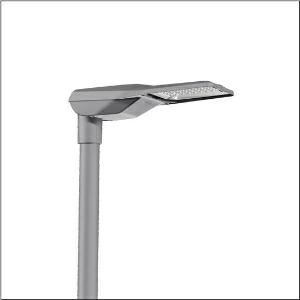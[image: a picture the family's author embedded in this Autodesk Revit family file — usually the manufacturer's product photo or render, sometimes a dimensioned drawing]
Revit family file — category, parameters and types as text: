
# Revit family: streetlight_sl_21_mini___st1_5a_5xe6p43a08hb_28db
name_source: partatom
category: Lighting Fixtures
units: mm (PartAtom-declared; Revit-internal decimal feet)

## family parameters
Cut with Voids When Loaded = No
Host = Face
Light Source = No
Part Type = Normal
Room Calculation Point = No
Round Connector Dimension = Use Diameter
Shared = No

## types (1)
- --- (1 x LED, 9260 lm, 66 W, 4000K)
    Apparent Load = 66 VA
    CIE Flux Codes = 22 53 95 100 100
    Color Rendering = 70
    Color Temperature = 4000K
    Default Elevation = 1800 mm
    Description = Streetlight SL 21 mini, mast luminaire, primary light control with lens, of PMMA, primary optical cover: cover, of toughened safety glass, transparent, light distribution: ST1.5a, light emission: direct distribution, primary light characteristic: asymmetric, installation type: post-top, side-entry, LED, 3G 1.5mm², High Power LED, rated luminous flux: 9.260lm, luminous efficacy: 140lm/W, light colour: 740, colour temperature: 4000K, control: overheat protection, constant luminous flux control, time-dependent luminous flux control, flexible luminous flux parameterisation, mains connection: 230..240V, AC, 50/60Hz, connection cable pre-assembled, cable length: 8,5m, wiring characteristics: H07RN-F, start of lifetime: 66W, end of service life: 69W, reduction: 30W, luminaire housing, of diecast aluminium, powder-coated, Siteco® metallic grey (DB 702S), corrosivity category C5 mid according to DIN EN ISO 12944, please order mast flange separately, inclination adjustable: 0°, 5°, 10°, 15°, sealing non-destructively replaceable, multi-level sealing system, length: 628mm, width: 235mm, height: 110mm, mast flange for spigot size: 42mm (side-entry): 5XC10008XM4, 60/48mm (side-entry/post-top): 5XC10108XM2, 76/60mm (side-entry/post-top): 5XC10108XM1, protection rating (complete): IP66, insulation class (complete): insulation class II (safety insulation), certification: CE, ENEC, ENEC+, VDE, impact resistance: IK09, permissible operating ambient temperature for outdoor applications: -40..+50°C, standard-compliant lighting for roads and squares, packaging unit: 1 piece

Light Distribution: ST1.5a
    Height = 110 mm
    Lamp = 1 x LED
    Lamp Light Flux = 9260 lm
    Lamp Power = 66 W
    Lamp count = 1
    Length = 625 mm
    Luminous efficacy = 140 lm/W
    Manufacturer = Siteco
    ModVariant = No
    Model = 5XE6P43A08HB
    Number of Poles = 1
    OnlyDefault = Yes
    Power Factor = 1
    Product Name = Streetlight SL 21 mini | ST1.5a
    Product group = mast luminaire | pylon top
    ProductGroupID = 6100
    Protection Class = Protection class II
    Protection Degree = IP 66
    RLX_Detail_Level = 1
    RLX_Emergency_Light_Flux = 0 lm
    RLX_Emergency_Type = 0
    RLX_Emergency_Type_DB = No
    RlxData = <blob elided: 95465 chars, md5=984b1427>
    Socket = socket
    Standby Power = 0 W
    System Light Flux = 9260 lm
    System Power = 66 W
    Type Comments = factory setting: luminous flux: 100 % | Output Level: 100 % | 670 mA
    Type Image = l_1003519.jpg
    URL = http://relux.com
    VarID = @adj_108529
    Voltage = 0 V
    Weight = 0.00 kg
    Width = 234 mm

## geometry (parser evidence)
native form markers: Blend x4, Sweep x10
no freeform markers — native parametric forms only
